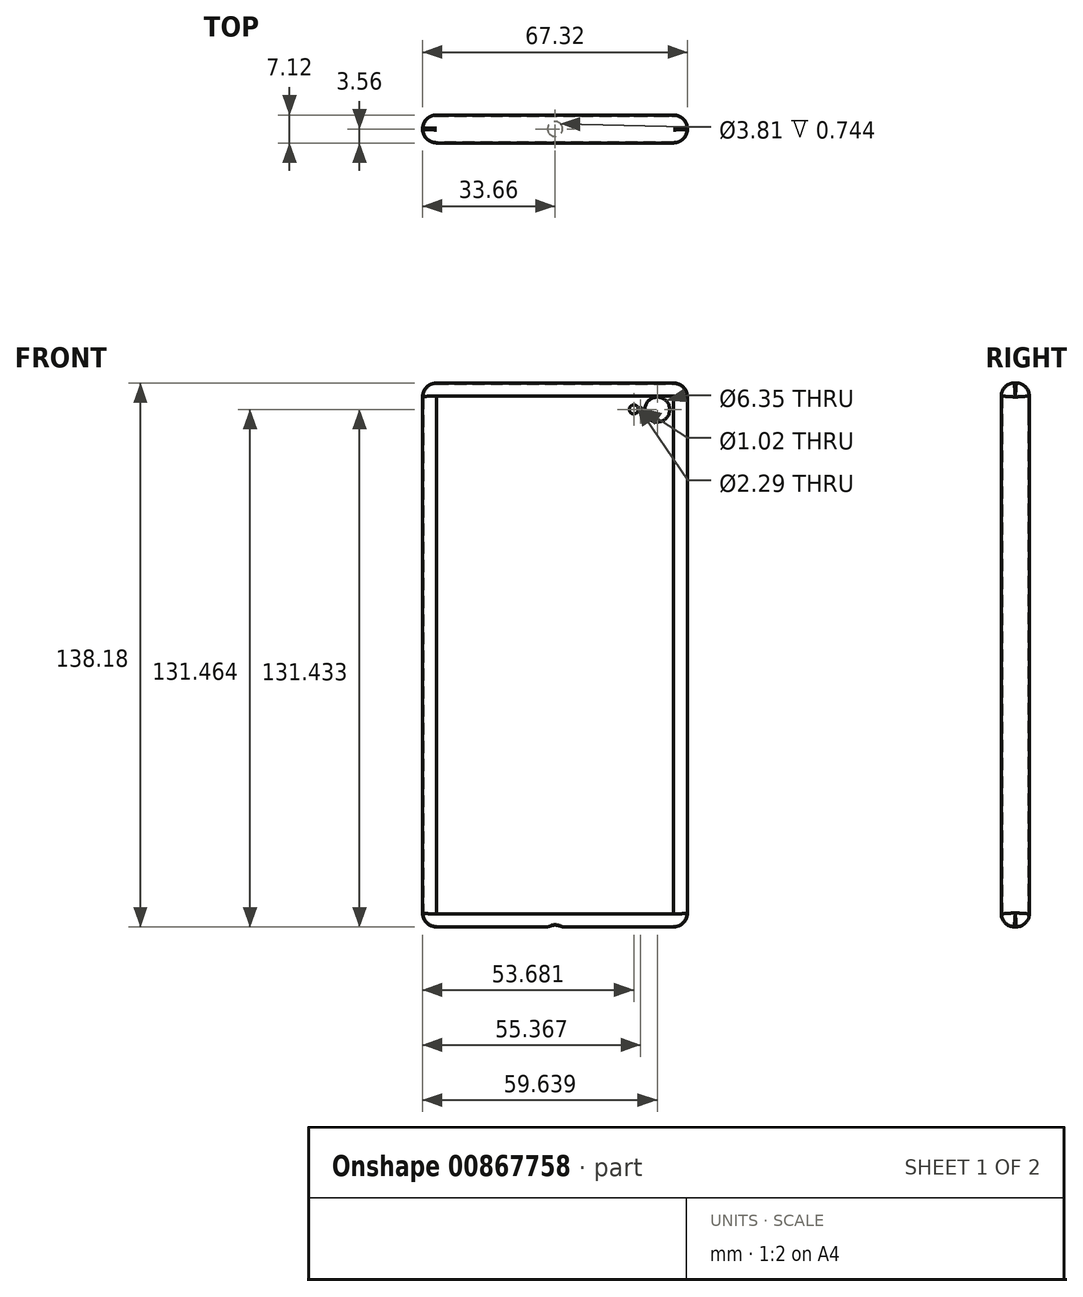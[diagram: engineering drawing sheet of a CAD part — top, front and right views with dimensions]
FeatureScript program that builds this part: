
annotation { "Feature Type Name" : "Feature", "Feature Type Description" : "" }
export const myFeature = defineFeature(function(context is Context, id is Id, definition is map)
    precondition{}
    {
        {
            var Q0;
            Q0=qCreatedBy(makeId("Front.planeOp"),FACE);
            var sketch = newSketch(context, id + "F0", { "sketchPlane" : qUnion([Q0])});
            skLineSegment(sketch, "E0.bottom", {"start": v(-33.65, 69.09) * mm, "end": v(33.66, 69.09) * mm});
            skLineSegment(sketch, "E0.top", {"start": v(-33.66, -69.09) * mm, "end": v(33.65, -69.09) * mm});
            skLineSegment(sketch, "E0.left", {"start": v(-33.65, 69.09) * mm, "end": v(-33.66, -69.09) * mm});
            skLineSegment(sketch, "E0.right", {"start": v(33.66, 69.09) * mm, "end": v(33.65, -69.09) * mm});
            skPoint(sketch, "E0.middle", {"position": v(0, 0) * mm});
            skSolve(sketch);
        }
        {
            var Q0;
            Q0=makeQuery(id+"F0.imprint","IMPRINT",FACE,{"disambiguationData":[TD([[makeQuery(id+"F0.imprint","IMPRINT",EDGE,{"derivedFrom":sQuery(id+"F0.wireOp",EDGE,"E0.bottom")}),-1.0]])]});
            extrude(context, id + "F1", {"entities" : qUnion([Q0]), "endBound" : BoundingType.SYMMETRIC, "depth" : 7.11 * mm, "offsetDistance" : 25.4 * mm});
        }
        {
            var Q0;
            Q0=makeQuery(id+"F1.opExtrude","CAP_EDGE",EDGE,{"disambiguationData":[OSD([sQuery(id+"F0.wireOp",EDGE,"E0.bottom")])],"isStart":false});
            var Q1;
            Q1=makeQuery(id+"F1.opExtrude","CAP_EDGE",EDGE,{"disambiguationData":[OSD([sQuery(id+"F0.wireOp",EDGE,"E0.bottom")])],"isStart":true});
            var Q2;
            Q2=makeQuery(id+"F1.opExtrude","CAP_EDGE",EDGE,{"disambiguationData":[OSD([sQuery(id+"F0.wireOp",EDGE,"E0.top")])],"isStart":false});
            var Q3;
            Q3=makeQuery(id+"F1.opExtrude","CAP_EDGE",EDGE,{"disambiguationData":[OSD([sQuery(id+"F0.wireOp",EDGE,"E0.top")])],"isStart":true});
            fillet(context, id + "F2", {"entities" : qUnion([Q0, Q1, Q2, Q3]), "radius" : 3.3 * mm, "tangentPropagation" : true, "allowEdgeOverflow" : false});
        }
        {
            var Q0;
            Q0=makeQuery(id+"F1.opExtrude","CAP_EDGE",EDGE,{"disambiguationData":[OSD([sQuery(id+"F0.wireOp",EDGE,"E0.left")])],"isStart":false});
            var Q1;
            Q1=makeQuery(id+"F1.opExtrude","CAP_EDGE",EDGE,{"disambiguationData":[OSD([sQuery(id+"F0.wireOp",EDGE,"E0.left")])],"isStart":true});
            var Q2;
            Q2=makeQuery(id+"F1.opExtrude","CAP_EDGE",EDGE,{"disambiguationData":[OSD([sQuery(id+"F0.wireOp",EDGE,"E0.right")])],"isStart":true});
            var Q3;
            Q3=makeQuery(id+"F1.opExtrude","CAP_EDGE",EDGE,{"disambiguationData":[OSD([sQuery(id+"F0.wireOp",EDGE,"E0.right")])],"isStart":false});
            fillet(context, id + "F3", {"entities" : qUnion([Q0, Q1, Q2, Q3]), "radius" : 3.56 * mm, "tangentPropagation" : true, "allowEdgeOverflow" : false});
        }
        {
            var Q0;
            Q0=makeQuery(id+"F1.opExtrude","CAP_FACE",FACE,{"disambiguationData":[OSD([sQuery(id+"F0.wireOp",EDGE,"E0.bottom"),sQuery(id+"F0.wireOp",EDGE,"E0.top"),sQuery(id+"F0.wireOp",EDGE,"E0.left"),sQuery(id+"F0.wireOp",EDGE,"E0.right")])],"isStart":false});
            shell(context, id + "F4", {"entities" : qUnion([Q0]), "thickness" : 0.25 * mm});
        }
        {
            var Q0;
            Q0=makeQuery(id+"F1.opExtrude","CAP_FACE",FACE,{"disambiguationData":[OSD([sQuery(id+"F0.wireOp",EDGE,"E0.bottom"),sQuery(id+"F0.wireOp",EDGE,"E0.top"),sQuery(id+"F0.wireOp",EDGE,"E0.left"),sQuery(id+"F0.wireOp",EDGE,"E0.right")])],"isStart":true});
            var sketch = newSketch(context, id + "F5", { "sketchPlane" : qUnion([Q0])});
            skPoint(sketch, "E1", {"position": v(-25.98, 62.34) * mm});
            skSolve(sketch);
        }
        {
            var Q0;
            Q0=sQuery(id+"F5.wireOp",VERTEX,"E1");
            var Q1;
            Q1=makeQuery(id+"F1.opExtrude","SWEPT_BODY",BODY,{"disambiguationData":[OSD([sQuery(id+"F0.wireOp",EDGE,"E0.bottom"),sQuery(id+"F0.wireOp",EDGE,"E0.top"),sQuery(id+"F0.wireOp",EDGE,"E0.left"),sQuery(id+"F0.wireOp",EDGE,"E0.right")])]});
            hole(context, id + "F6", {"style" : HoleStyle.SIMPLE, "endStyle" : HoleEndStyle.THROUGH, "holeDiameter" : 6.35 * mm, "majorDiameter" : 6.35 * mm, "isTappedThrough" : true, "tappedDepth" : 12.7 * mm, "tapClearance" : 3, "locations" : qUnion([Q0]), "scope" : qUnion([Q1])});
        }
        {
            var Q0;
            {var subQ0=sQuery(id+"F0.wireOp",EDGE,"E0.right");var subQ1=sQuery(id+"F0.wireOp",EDGE,"E0.left");var subQ2=sQuery(id+"F0.wireOp",EDGE,"E0.top");var subQ3=sQuery(id+"F0.wireOp",EDGE,"E0.bottom");var subQ4=makeQuery(id+"F1.opExtrude","CAP_FACE",FACE,{"disambiguationData":[OSD([subQ3,subQ2,subQ1,subQ0])],"isStart":true});Q0=makeQuery(id+"F5.imprint","IMPRINT",FACE,{"disambiguationData":[TD([[makeQuery(id+"F5.imprint","IMPRINT",EDGE,{"derivedFrom":makeQuery(id+"F2.opFillet","BLEND_EDGE",EDGE,{"blendedFrom":[makeQuery(id+"F1.opExtrude","CAP_EDGE",EDGE,{"disambiguationData":[OSD([subQ3])],"isStart":true}),subQ4],"blendedInto":[subQ4]})}),1.0]])]});}
            var sketch = newSketch(context, id + "F7", { "sketchPlane" : qUnion([Q0])});
            skPoint(sketch, "E2", {"position": v(-21.7, 62.34) * mm});
            skSolve(sketch);
        }
        {
            var Q0;
            Q0=sQuery(id+"F7.wireOp",VERTEX,"E2");
            var Q1;
            Q1=makeQuery(id+"F1.opExtrude","SWEPT_BODY",BODY,{"disambiguationData":[OSD([sQuery(id+"F0.wireOp",EDGE,"E0.bottom"),sQuery(id+"F0.wireOp",EDGE,"E0.top"),sQuery(id+"F0.wireOp",EDGE,"E0.left"),sQuery(id+"F0.wireOp",EDGE,"E0.right")])]});
            hole(context, id + "F8", {"style" : HoleStyle.SIMPLE, "endStyle" : HoleEndStyle.THROUGH, "holeDiameter" : 1.02 * mm, "majorDiameter" : 6.35 * mm, "isTappedThrough" : true, "tappedDepth" : 12.7 * mm, "tapClearance" : 3, "locations" : qUnion([Q0]), "scope" : qUnion([Q1])});
        }
        {
            var Q0;
            {var subQ0=sQuery(id+"F0.wireOp",EDGE,"E0.right");var subQ1=sQuery(id+"F0.wireOp",EDGE,"E0.left");var subQ2=sQuery(id+"F0.wireOp",EDGE,"E0.top");var subQ3=sQuery(id+"F0.wireOp",EDGE,"E0.bottom");var subQ4=makeQuery(id+"F1.opExtrude","CAP_FACE",FACE,{"disambiguationData":[OSD([subQ3,subQ2,subQ1,subQ0])],"isStart":true});Q0=makeQuery(id+"F5.imprint","IMPRINT",FACE,{"disambiguationData":[TD([[makeQuery(id+"F5.imprint","IMPRINT",EDGE,{"derivedFrom":makeQuery(id+"F2.opFillet","BLEND_EDGE",EDGE,{"blendedFrom":[makeQuery(id+"F1.opExtrude","CAP_EDGE",EDGE,{"disambiguationData":[OSD([subQ3])],"isStart":true}),subQ4],"blendedInto":[subQ4]})}),1.0]])]});}
            var sketch = newSketch(context, id + "F9", { "sketchPlane" : qUnion([Q0])});
            skPoint(sketch, "E3", {"position": v(-20.02, 62.37) * mm});
            skSolve(sketch);
        }
        {
            var Q0;
            Q0=sQuery(id+"F9.wireOp",VERTEX,"E3");
            var Q1;
            Q1=makeQuery(id+"F1.opExtrude","SWEPT_BODY",BODY,{"disambiguationData":[OSD([sQuery(id+"F0.wireOp",EDGE,"E0.bottom"),sQuery(id+"F0.wireOp",EDGE,"E0.top"),sQuery(id+"F0.wireOp",EDGE,"E0.left"),sQuery(id+"F0.wireOp",EDGE,"E0.right")])]});
            hole(context, id + "F10", {"style" : HoleStyle.SIMPLE, "endStyle" : HoleEndStyle.THROUGH, "holeDiameter" : 2.3 * mm, "majorDiameter" : 6.35 * mm, "isTappedThrough" : true, "tappedDepth" : 12.7 * mm, "tapClearance" : 3, "locations" : qUnion([Q0]), "scope" : qUnion([Q1])});
        }
        {
            var Q0;
            Q0=makeQuery(id+"F1.opExtrude","SWEPT_FACE",FACE,{"disambiguationData":[OSD([sQuery(id+"F0.wireOp",EDGE,"E0.top")])]});
            var sketch = newSketch(context, id + "F11", { "sketchPlane" : qUnion([Q0])});
            skPoint(sketch, "E4", {"position": v(0, 0) * mm});
            skSolve(sketch);
        }
        {
            var Q0;
            Q0=sQuery(id+"F11.wireOp",VERTEX,"E4");
            var Q1;
            Q1=makeQuery(id+"F1.opExtrude","SWEPT_BODY",BODY,{"disambiguationData":[OSD([sQuery(id+"F0.wireOp",EDGE,"E0.bottom"),sQuery(id+"F0.wireOp",EDGE,"E0.top"),sQuery(id+"F0.wireOp",EDGE,"E0.left"),sQuery(id+"F0.wireOp",EDGE,"E0.right")])]});
            hole(context, id + "F12", {"style" : HoleStyle.SIMPLE, "endStyle" : HoleEndStyle.BLIND, "holeDiameter" : 3.8 * mm, "majorDiameter" : 6.35 * mm, "holeDepth" : 1.27 * mm, "isTappedThrough" : true, "tappedDepth" : 12.7 * mm, "tapClearance" : 3, "locations" : qUnion([Q0]), "scope" : qUnion([Q1])});
        }
    });
